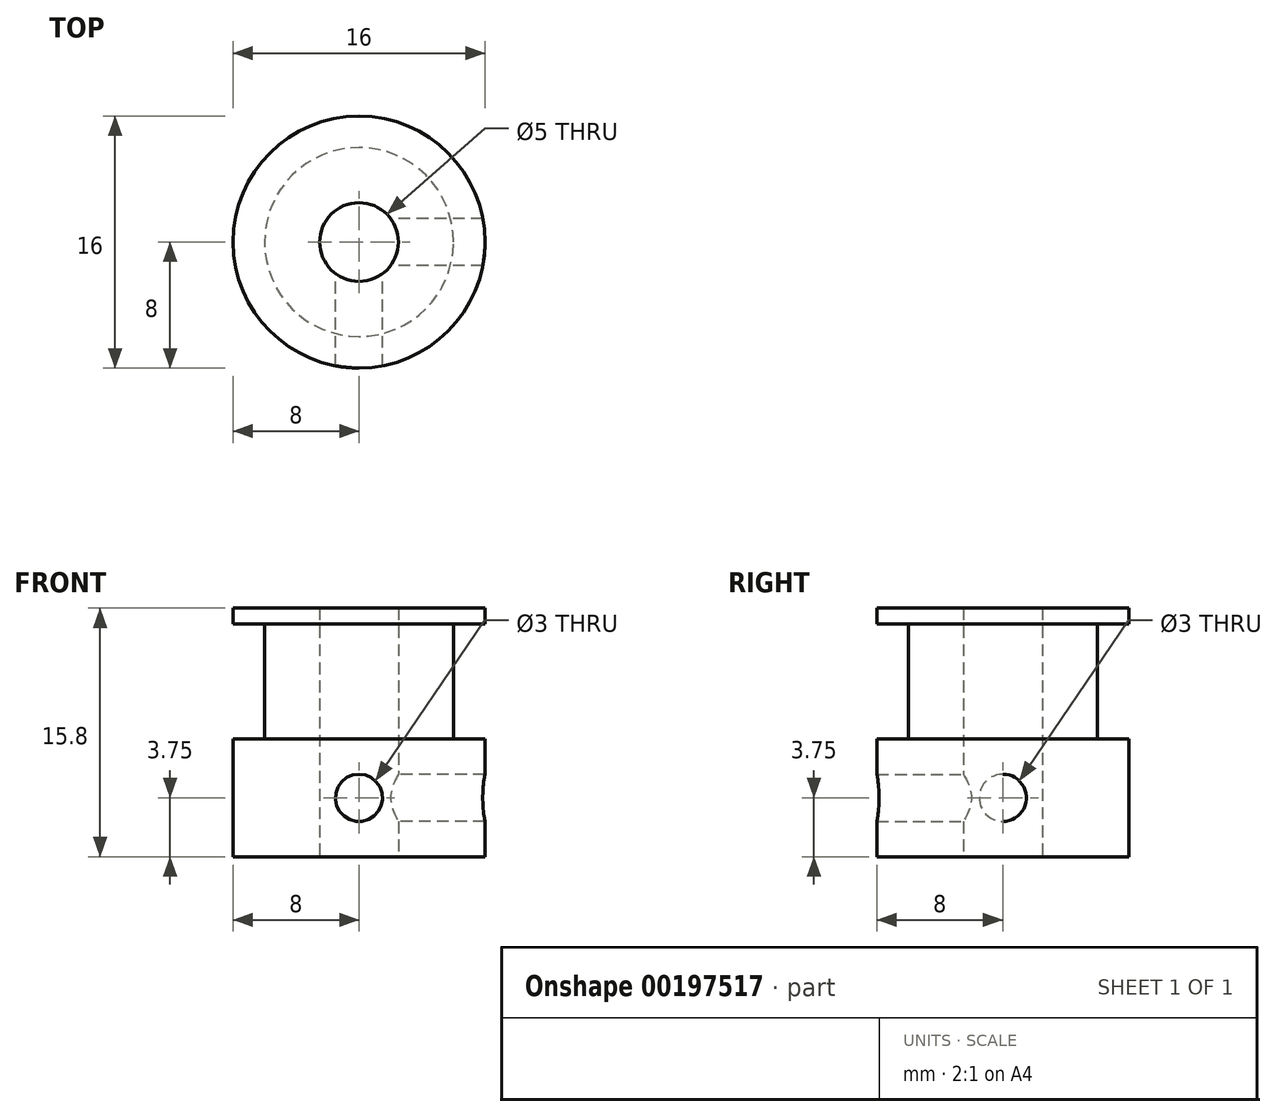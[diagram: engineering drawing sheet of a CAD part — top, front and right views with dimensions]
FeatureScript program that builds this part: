
annotation { "Feature Type Name" : "Feature", "Feature Type Description" : "" }
export const myFeature = defineFeature(function(context is Context, id is Id, definition is map)
    precondition{}
    {
        {
            var Q0;
            Q0=qCreatedBy(makeId("Top.planeOp"),FACE);
            var sketch = newSketch(context, id + "F0", { "sketchPlane" : qUnion([Q0])});
            skCircle(sketch, "E0", {"center": v(0, 0) * mm, "radius": 8 * mm});
            skCircle(sketch, "E1", {"center": v(0, 0) * mm, "radius": 2.5 * mm});
            skSolve(sketch);
        }
        {
            var Q0;
            Q0=qSketchRegion(id+"F0",true);
            extrude(context, id + "F1", {"entities" : qUnion([Q0]), "depth" : 7.5 * mm});
        }
        {
            var Q0;
            Q0=makeQuery(id+"F1.opExtrude","CAP_FACE",FACE,{"disambiguationData":[OSD([sQuery(id+"F0.wireOp",EDGE,"E0"),sQuery(id+"F0.wireOp",EDGE,"E1")])],"isStart":false});
            var sketch = newSketch(context, id + "F2", { "sketchPlane" : qUnion([Q0])});
            skCircle(sketch, "E2", {"center": v(0, 0) * mm, "radius": 6 * mm});
            skCircle(sketch, "E3.0", {"center": v(0, 0) * mm, "radius": 2.5 * mm});
            skSolve(sketch);
        }
        {
            var Q0;
            Q0=qSketchRegion(id+"F2",true);
            extrude(context, id + "F3", {"entities" : qUnion([Q0]), "operationType" : NewBodyOperationType.ADD, "depth" : 7.3 * mm});
        }
        {
            var Q0;
            Q0=makeQuery(id+"F3.opExtrude","CAP_FACE",FACE,{"disambiguationData":[OSD([sQuery(id+"F2.wireOp",EDGE,"E2"),sQuery(id+"F2.wireOp",EDGE,"E3.0")])],"isStart":false});
            var sketch = newSketch(context, id + "F4", { "sketchPlane" : qUnion([Q0])});
            skCircle(sketch, "E4.0", {"center": v(0, 0) * mm, "radius": 8 * mm});
            skCircle(sketch, "E4.1", {"center": v(0, 0) * mm, "radius": 2.5 * mm});
            skSolve(sketch);
        }
        {
            var Q0;
            Q0=qSketchRegion(id+"F4",true);
            extrude(context, id + "F5", {"entities" : qUnion([Q0]), "operationType" : NewBodyOperationType.ADD, "depth" : 1 * mm});
        }
        {
            var Q0;
            Q0=qCreatedBy(makeId("Front.planeOp"),FACE);
            var sketch = newSketch(context, id + "F6", { "sketchPlane" : qUnion([Q0])});
            skCircle(sketch, "E5", {"center": v(0, 3.75) * mm, "radius": 1.5 * mm});
            skSolve(sketch);
        }
        {
            var Q0;
            Q0=qSketchRegion(id+"F6",true);
            extrude(context, id + "F7", {"entities" : qUnion([Q0]), "operationType" : NewBodyOperationType.REMOVE, "depth" : 8 * mm});
        }
        {
            var Q0;
            Q0=qCreatedBy(makeId("Right.planeOp"),FACE);
            var sketch = newSketch(context, id + "F8", { "sketchPlane" : qUnion([Q0])});
            skCircle(sketch, "E6", {"center": v(0, 3.75) * mm, "radius": 1.5 * mm});
            skSolve(sketch);
        }
        {
            var Q0;
            Q0=qSketchRegion(id+"F8",true);
            extrude(context, id + "F9", {"entities" : qUnion([Q0]), "operationType" : NewBodyOperationType.REMOVE, "depth" : 8 * mm});
        }
    });
